# Revit family: 2-5142-24 Zenith
name_source: partatom
category: Lighting Fixtures
revit_build: Autodesk Revit LT 2014 (Build: 20130308_1515(x64)
units: mm (PartAtom-declared; Revit-internal decimal feet)

## types (1)
- 2-5142-24 Zenith
    ADA Compliant = No
    Apparent Load = 31 VA
    Ballast Manufacturer = Antron Electronics ESD-A35T5
    Color Filter = 16777215
    Default Elevation = 4' - 0"
    Description = 48" Vanity - 1xT-5 linear fluorescent
    Diffuser = Acrylic- Matte White
    Dimming Lamp Color Temperature Shift = <None>
    Emit Shape Visible in Rendering = No
    Emit from Rectangle Length = 4' - 0"
    Emit from Rectangle Width = 2' - 0"
    Fixture Height = 0' - 3 1/16"
    Fixture Length = 3' - 11 5/8"
    Input Power (Watts) = 31 W
    Input Voltage (VAC) = 120.0
    Junction Box = 2"x3" Junction Box
    Lamp = 1x28W T-5 FP28/841/ECO Linear Fluorescent
    Lamp Manufacturer = Sylvania
    Manufacturer = Oxygen Lighting
    Metal Finish = Satin Nickel
    Model = 2-5142-24
    Photometric Web File = 2-5142-24 Zenith 48 ITL77183.IES
    Power Factor = 0.99
    Product Documentation Link = http://oxygenlighting.com.s3.amazonaws.com
    Tilt Angle = 180.00°
    Type Comments = Lighting - Fluorescent
    URL = http://www.oxygenlighting.com

## geometry (parser evidence)
native form markers: Sweep x1
no freeform markers — native parametric forms only
